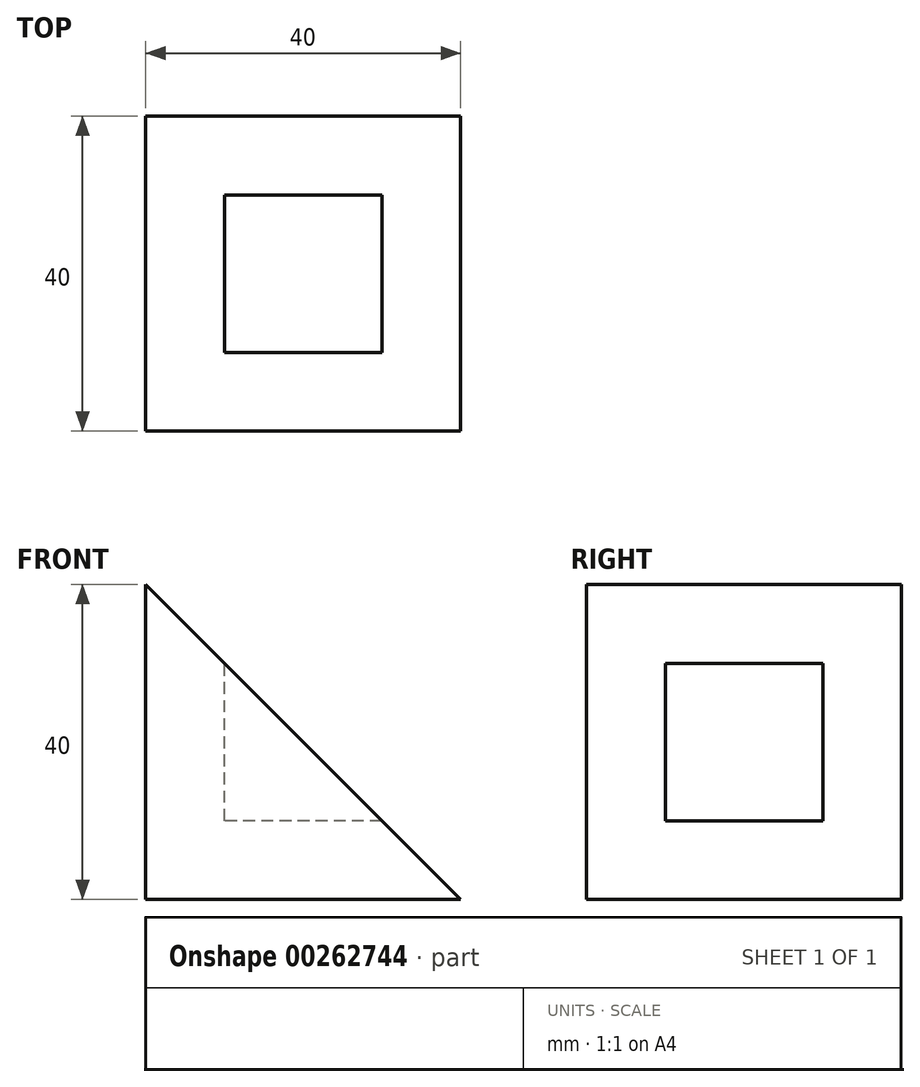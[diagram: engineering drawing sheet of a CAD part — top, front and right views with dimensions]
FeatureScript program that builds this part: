
annotation { "Feature Type Name" : "Feature", "Feature Type Description" : "" }
export const myFeature = defineFeature(function(context is Context, id is Id, definition is map)
    precondition{}
    {
        {
            var Q0;
            Q0=qCreatedBy(makeId("Front.planeOp"),FACE);
            var sketch = newSketch(context, id + "F0", { "sketchPlane" : qUnion([Q0])});
            skLineSegment(sketch, "E0", {"start": v(0, 0) * mm, "end": v(0, 40) * mm});
            skLineSegment(sketch, "E1", {"start": v(0, 40) * mm, "end": v(40, 0) * mm});
            skLineSegment(sketch, "E2", {"start": v(40, 0) * mm, "end": v(0, 0) * mm});
            skSolve(sketch);
        }
        {
            var Q0;
            Q0 = qSketchRegion(id + "F0", true);
            extrude(context, id + "F1", {"entities" : qUnion([Q0]), "depth" : 40 * mm});
        }
        {
            var Q0;
            Q0=qCreatedBy(makeId("Right.planeOp"),FACE);
            cPlane(context, id + "F2", {"entities" : qUnion([Q0]), "cplaneType" : CPlaneType.OFFSET, "offset" : 10 * mm, "width" : 150 * mm, "height" : 150 * mm});
        }
        {
            var Q0;
            Q0=qCreatedBy(id+"F2.planeOp",FACE);
            var sketch = newSketch(context, id + "F3", { "sketchPlane" : qUnion([Q0])});
            skLineSegment(sketch, "E3.bottom", {"start": v(0, 0) * mm, "end": v(-10, 0) * mm, "construction": true});
            skLineSegment(sketch, "E3.top", {"start": v(0, 10) * mm, "end": v(-10, 10) * mm, "construction": true});
            skLineSegment(sketch, "E3.left", {"start": v(0, 0) * mm, "end": v(0, 10) * mm, "construction": true});
            skLineSegment(sketch, "E3.right", {"start": v(-10, 0) * mm, "end": v(-10, 10) * mm, "construction": true});
            skLineSegment(sketch, "E4.bottom", {"start": v(-10, 10) * mm, "end": v(-30, 10) * mm});
            skLineSegment(sketch, "E4.top", {"start": v(-10, 40) * mm, "end": v(-30, 40) * mm});
            skLineSegment(sketch, "E4.left", {"start": v(-10, 10) * mm, "end": v(-10, 40) * mm});
            skLineSegment(sketch, "E4.right", {"start": v(-30, 10) * mm, "end": v(-30, 40) * mm});
            skSolve(sketch);
        }
        {
            var Q0;
            Q0 = qSketchRegion(id + "F3", true);
            extrude(context, id + "F4", {"entities" : qUnion([Q0]), "operationType" : NewBodyOperationType.REMOVE, "depth" : 25 * mm});
        }
    });
